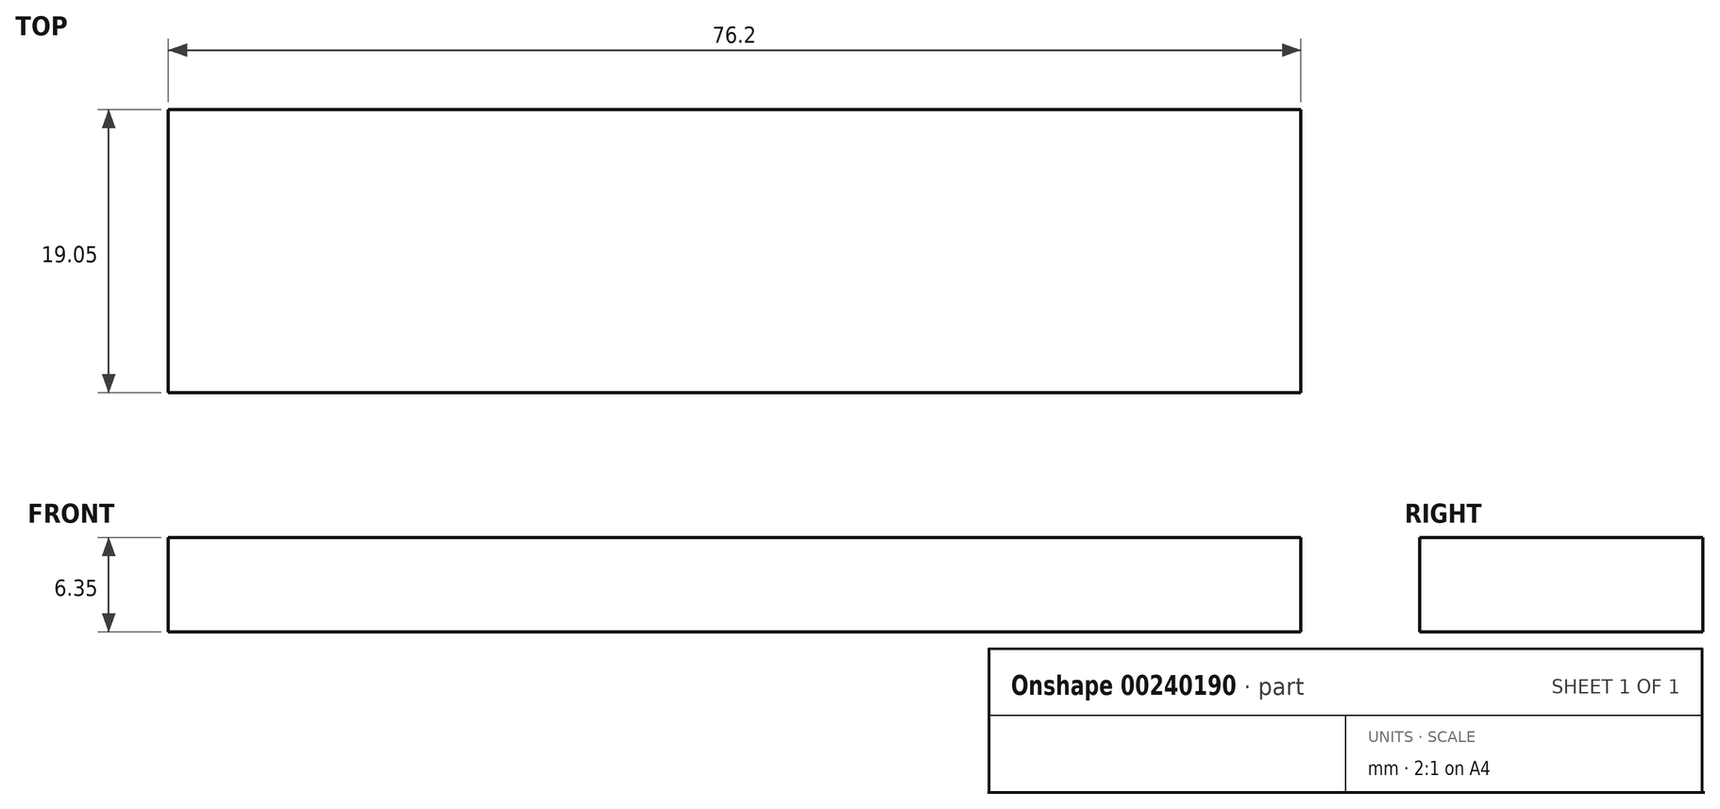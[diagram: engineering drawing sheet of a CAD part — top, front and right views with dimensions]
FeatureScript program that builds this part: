
annotation { "Feature Type Name" : "Feature", "Feature Type Description" : "" }
export const myFeature = defineFeature(function(context is Context, id is Id, definition is map)
    precondition{}
    {
        {
            var Q0;
            Q0=qCreatedBy(makeId("Top.planeOp"),FACE);
            var sketch = newSketch(context, id + "F0", { "sketchPlane" : qUnion([Q0])});
            skLineSegment(sketch, "E0.bottom", {"start": v(-33.14, -1.38) * mm, "end": v(43.06, -1.38) * mm});
            skLineSegment(sketch, "E0.top", {"start": v(-33.14, -20.43) * mm, "end": v(43.06, -20.43) * mm});
            skLineSegment(sketch, "E0.left", {"start": v(-33.14, -1.38) * mm, "end": v(-33.14, -20.43) * mm});
            skLineSegment(sketch, "E0.right", {"start": v(43.06, -1.38) * mm, "end": v(43.06, -20.43) * mm});
            skSolve(sketch);
        }
        {
            var Q0;
            Q0=makeQuery(id+"F0.imprint","IMPRINT",FACE,{"disambiguationData":[TD([[makeQuery(id+"F0.imprint","IMPRINT",EDGE,{"derivedFrom":sQuery(id+"F0.wireOp",EDGE,"E0.bottom")}),-1.0]])]});
            extrude(context, id + "F1", {"entities" : qUnion([Q0]), "depth" : 6.35 * mm});
        }
    });
